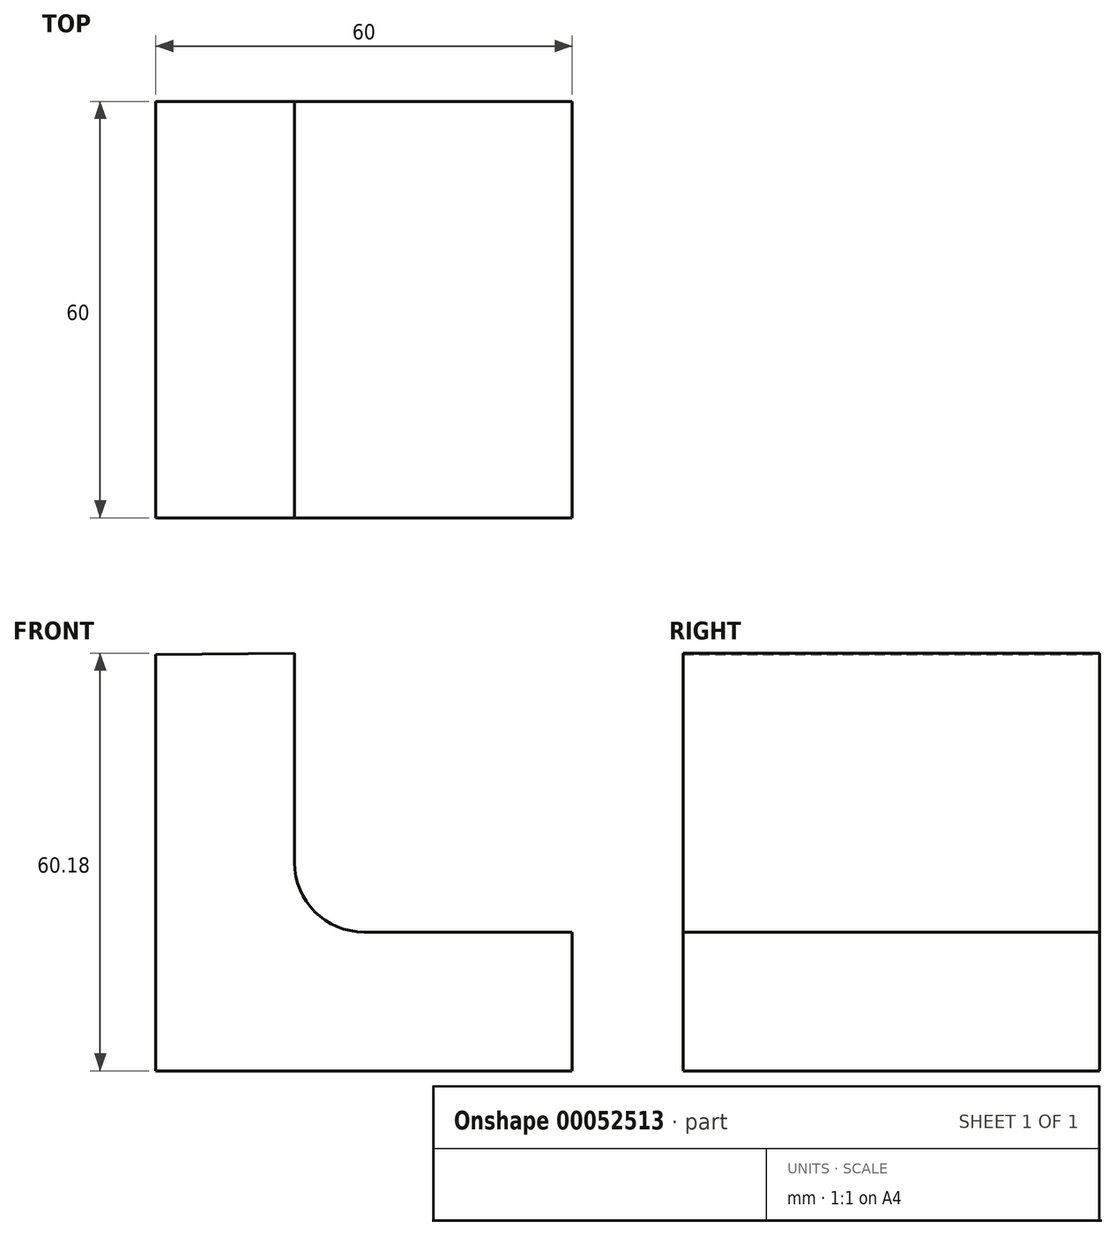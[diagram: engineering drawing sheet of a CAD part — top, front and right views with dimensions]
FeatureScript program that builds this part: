
annotation { "Feature Type Name" : "Feature", "Feature Type Description" : "" }
export const myFeature = defineFeature(function(context is Context, id is Id, definition is map)
    precondition{}
    {
        {
            var Q0;
            Q0=qCreatedBy(makeId("Front.planeOp"),FACE);
            var sketch = newSketch(context, id + "F0", { "sketchPlane" : qUnion([Q0])});
            skLineSegment(sketch, "E0", {"start": v(-35.97, 30.49) * mm, "end": v(-35.97, -29.51) * mm});
            skLineSegment(sketch, "E1", {"start": v(-35.97, -29.51) * mm, "end": v(24.03, -29.51) * mm});
            skLineSegment(sketch, "E2", {"start": v(24.03, -29.51) * mm, "end": v(24.03, -9.51) * mm});
            skLineSegment(sketch, "E3", {"start": v(24.03, -9.51) * mm, "end": v(-5.98, -9.51) * mm});
            skLineSegment(sketch, "E4", {"start": v(-15.98, 0.49) * mm, "end": v(-15.98, 30.67) * mm});
            skLineSegment(sketch, "E5", {"start": v(-15.98, 30.67) * mm, "end": v(-35.97, 30.49) * mm});
            skPoint(sketch, "E6.visualSharp", {"position": v(-15.98, -9.51) * mm});
            skArc(sketch, "E6.filletArc", {"start": v(-15.98, 0.49) * mm, "mid": v(-13.05, -6.58) * mm, "end": v(-5.98, -9.51) * mm});
            skSolve(sketch);
        }
        {
            var Q0;
            Q0 = qSketchRegion(id + "F0", true);
            extrude(context, id + "F1", {"entities" : qUnion([Q0]), "depth" : 60 * mm});
        }
    });
